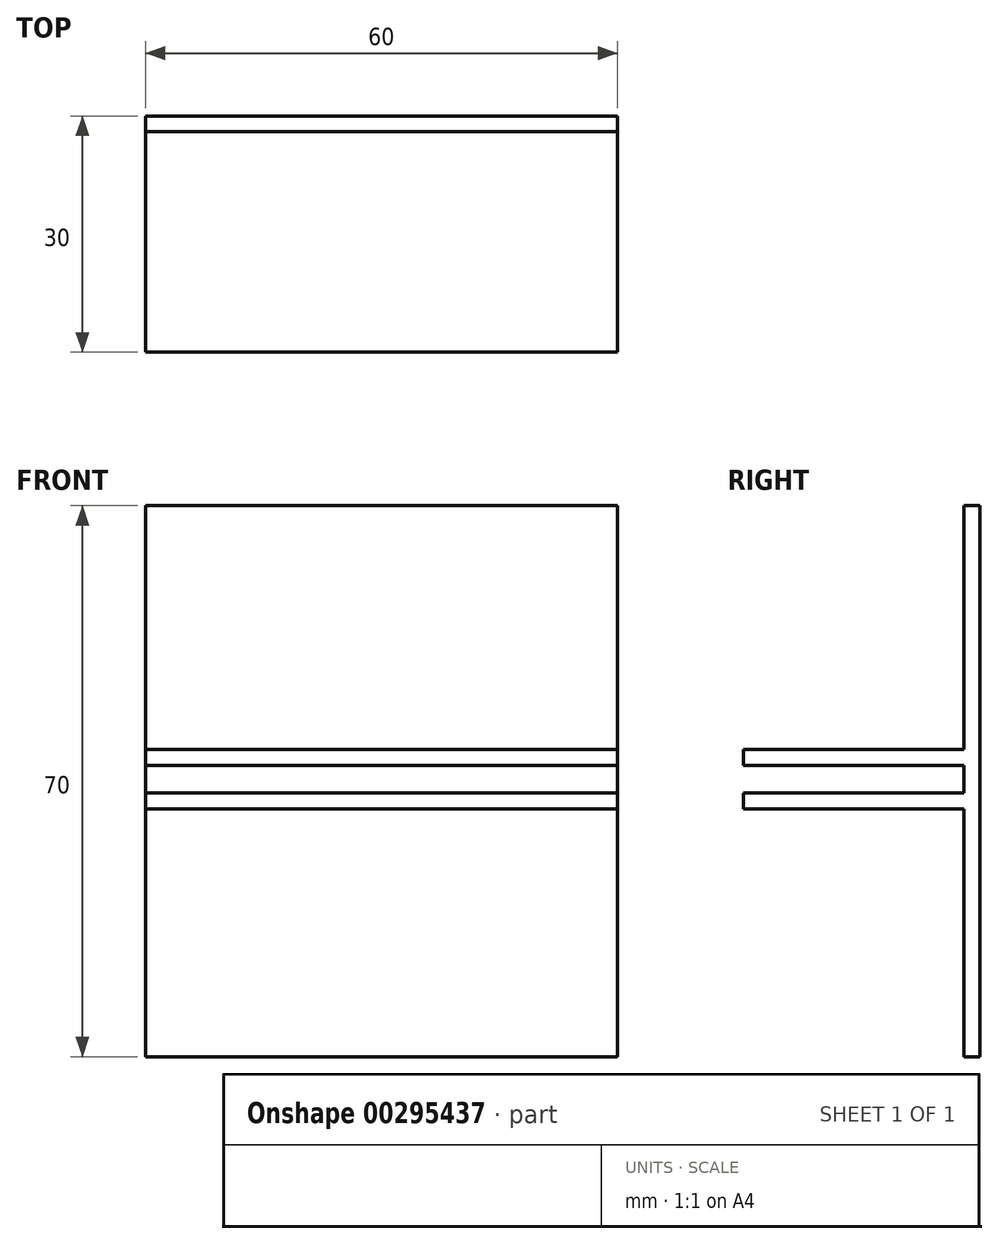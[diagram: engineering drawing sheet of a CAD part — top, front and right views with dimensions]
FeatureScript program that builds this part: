
annotation { "Feature Type Name" : "Feature", "Feature Type Description" : "" }
export const myFeature = defineFeature(function(context is Context, id is Id, definition is map)
    precondition{}
    {
        {
            var Q0;
            Q0=qCreatedBy(makeId("Front.planeOp"),FACE);
            var sketch = newSketch(context, id + "F0", { "sketchPlane" : qUnion([Q0])});
            skLineSegment(sketch, "E0.bottom", {"start": v(-30, 35) * mm, "end": v(30, 35) * mm});
            skLineSegment(sketch, "E0.top", {"start": v(-30, -35) * mm, "end": v(30, -35) * mm});
            skLineSegment(sketch, "E0.left", {"start": v(-30, 35) * mm, "end": v(-30, -35) * mm});
            skLineSegment(sketch, "E0.right", {"start": v(30, 35) * mm, "end": v(30, -35) * mm});
            skPoint(sketch, "E0.middle", {"position": v(0, 0) * mm});
            skLineSegment(sketch, "E1.bottom", {"start": v(-30, 4) * mm, "end": v(30, 4) * mm});
            skLineSegment(sketch, "E1.top", {"start": v(-30, 2) * mm, "end": v(30, 2) * mm});
            skLineSegment(sketch, "E1.left", {"start": v(-30, 4) * mm, "end": v(-30, 2) * mm});
            skLineSegment(sketch, "E1.right", {"start": v(30, 4) * mm, "end": v(30, 2) * mm});
            skLineSegment(sketch, "E2.bottom", {"start": v(-30, -1.5) * mm, "end": v(30, -1.5) * mm});
            skLineSegment(sketch, "E2.top", {"start": v(-30, -3.5) * mm, "end": v(30, -3.5) * mm});
            skLineSegment(sketch, "E2.left", {"start": v(-30, -1.5) * mm, "end": v(-30, -3.5) * mm});
            skLineSegment(sketch, "E2.right", {"start": v(30, -1.5) * mm, "end": v(30, -3.5) * mm});
            skSolve(sketch);
        }
        {
            var Q0;
            {var subQ0=sQuery(id+"F0.wireOp",EDGE,"E0.bottom");Q0=makeQuery(id+"F0.imprint","IMPRINT",FACE,{"disambiguationData":[TD([[makeQuery(id+"F0.imprint","IMPRINT",EDGE,{"derivedFrom":subQ0}),-1.0]])]});}
            var Q1;
            Q1=makeQuery(id+"F0.imprint","IMPRINT",FACE,{"disambiguationData":[TD([[makeQuery(id+"F0.imprint","IMPRINT",EDGE,{"derivedFrom":sQuery(id+"F0.wireOp",EDGE,"E1.bottom")}),-1.0]])]});
            var Q2;
            {var subQ0=sQuery(id+"F0.wireOp",EDGE,"E1.top");Q2=makeQuery(id+"F0.imprint","IMPRINT",FACE,{"disambiguationData":[TD([[makeQuery(id+"F0.imprint","IMPRINT",EDGE,{"derivedFrom":subQ0}),-1.0]])]});}
            var Q3;
            {var subQ0=sQuery(id+"F0.wireOp",EDGE,"E0.top");Q3=makeQuery(id+"F0.imprint","IMPRINT",FACE,{"disambiguationData":[TD([[makeQuery(id+"F0.imprint","IMPRINT",EDGE,{"derivedFrom":subQ0}),1.0]])]});}
            var Q4;
            Q4=makeQuery(id+"F0.imprint","IMPRINT",FACE,{"disambiguationData":[TD([[makeQuery(id+"F0.imprint","IMPRINT",EDGE,{"derivedFrom":sQuery(id+"F0.wireOp",EDGE,"E2.bottom")}),-1.0]])]});
            extrude(context, id + "F1", {"entities" : qUnion([Q0, Q1, Q2, Q3, Q4]), "depth" : 2 * mm});
        }
        {
            var Q0;
            Q0=makeQuery(id+"F0.imprint","IMPRINT",FACE,{"disambiguationData":[TD([[makeQuery(id+"F0.imprint","IMPRINT",EDGE,{"derivedFrom":sQuery(id+"F0.wireOp",EDGE,"E1.bottom")}),-1.0]])]});
            var Q1;
            Q1=makeQuery(id+"F0.imprint","IMPRINT",FACE,{"disambiguationData":[TD([[makeQuery(id+"F0.imprint","IMPRINT",EDGE,{"derivedFrom":sQuery(id+"F0.wireOp",EDGE,"E2.bottom")}),-1.0]])]});
            extrude(context, id + "F2", {"entities" : qUnion([Q0, Q1]), "operationType" : NewBodyOperationType.ADD, "depth" : 30 * mm});
        }
    });
